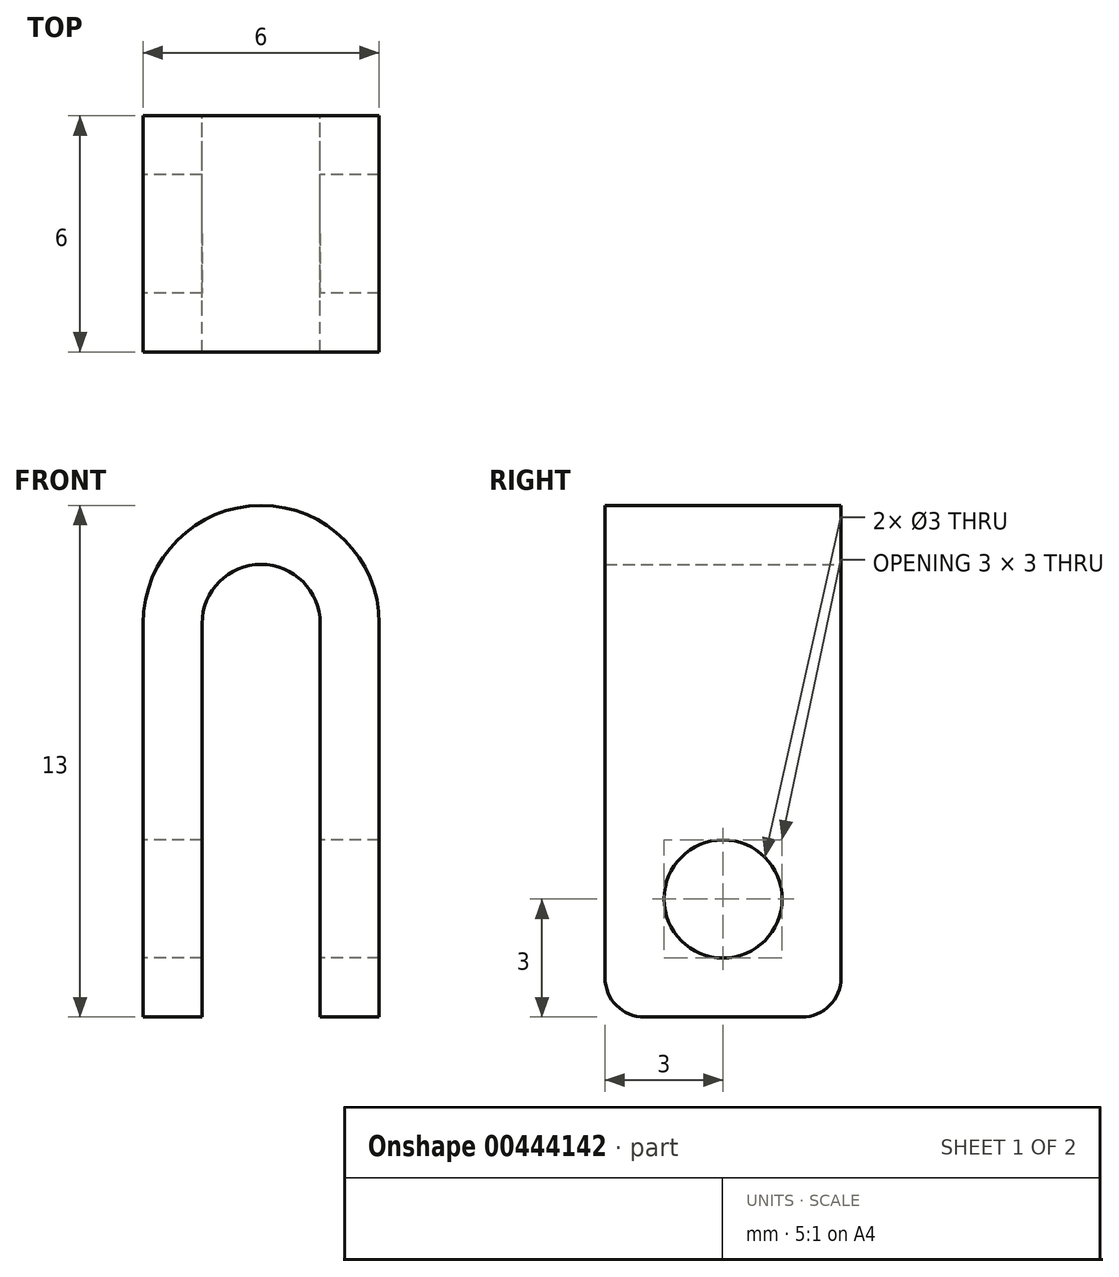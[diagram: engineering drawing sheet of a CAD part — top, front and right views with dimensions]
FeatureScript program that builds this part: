
annotation { "Feature Type Name" : "Feature", "Feature Type Description" : "" }
export const myFeature = defineFeature(function(context is Context, id is Id, definition is map)
    precondition{}
    {
        {
            var Q0;
            Q0=qCreatedBy(makeId("Front.planeOp"),FACE);
            var sketch = newSketch(context, id + "F0", { "sketchPlane" : qUnion([Q0])});
            skArc(sketch, "E0", {"start": v(-1.5, 0) * mm, "mid": v(0, 1.5) * mm, "end": v(1.5, 0) * mm});
            skArc(sketch, "E1", {"start": v(-3, 0) * mm, "mid": v(0, 3) * mm, "end": v(3, 0) * mm});
            skLineSegment(sketch, "E2", {"start": v(-1.5, 0) * mm, "end": v(-1.5, -10) * mm});
            skLineSegment(sketch, "E3", {"start": v(-3, -10) * mm, "end": v(-3, 0) * mm});
            skLineSegment(sketch, "E4", {"start": v(1.5, 0) * mm, "end": v(1.5, -10) * mm});
            skLineSegment(sketch, "E5", {"start": v(3, -10) * mm, "end": v(3, 0) * mm});
            skLineSegment(sketch, "E6", {"start": v(-3, -10) * mm, "end": v(-1.5, -10) * mm});
            skLineSegment(sketch, "E7", {"start": v(1.5, -10) * mm, "end": v(3, -10) * mm});
            skSolve(sketch);
        }
        {
            var Q0;
            Q0=makeQuery(id+"F0.imprint","IMPRINT",FACE,{"disambiguationData":[TD([[makeQuery(id+"F0.imprint","IMPRINT",EDGE,{"derivedFrom":sQuery(id+"F0.wireOp",EDGE,"E0")}),1.0]])]});
            var Q1;
            Q1=makeQuery(id+"F0.imprint","IMPRINT",FACE,{"disambiguationData":[TD([[makeQuery(id+"F0.imprint","IMPRINT",EDGE,{"derivedFrom":sQuery(id+"F0.wireOp",EDGE,"E0")}),-1.0]])]});
            var Q2;
            Q2=makeQuery(id+"F0.imprint","IMPRINT",FACE,{"disambiguationData":[TD([[makeQuery(id+"F0.imprint","IMPRINT",EDGE,{"derivedFrom":sQuery(id+"F0.wireOp",EDGE,"2HMxa7M1-go9X-fjSn-Mpx8-X3Mcg31AgzwF.bottom")}),-1.0]])]});
            var Q3;
            Q3=makeQuery(id+"F0.imprint","IMPRINT",FACE,{"disambiguationData":[TD([[makeQuery(id+"F0.imprint","IMPRINT",EDGE,{"derivedFrom":sQuery(id+"F0.wireOp",EDGE,"UYwaTrHf-vhDH-wfQa-s1mw-S1oxrttcXev8.bottom")}),1.0]])]});
            extrude(context, id + "F1", {"entities" : qUnion([Q0, Q1, Q2, Q3]), "depth" : 6 * mm});
        }
        {
            var Q0;
            Q0=makeQuery(id+"F1.opExtrude","SWEPT_FACE",FACE,{"disambiguationData":[OSD([sQuery(id+"F0.wireOp",EDGE,"E3")])]});
            var sketch = newSketch(context, id + "F2", { "sketchPlane" : qUnion([Q0])});
            skPoint(sketch, "E8", {"position": v(3, -7) * mm});
            skLineSegment(sketch, "E9.0.0", {"start": v(0, 0) * mm, "end": v(0, -10) * mm});
            skLineSegment(sketch, "E9.0.1", {"start": v(0, -10) * mm, "end": v(6, -10) * mm});
            skLineSegment(sketch, "E9.0.2", {"start": v(6, -10) * mm, "end": v(6, 0) * mm});
            skLineSegment(sketch, "E9.0.3", {"start": v(6, 0) * mm, "end": v(0, 0) * mm});
            skSolve(sketch);
        }
        {
            var Q0;
            Q0=sQuery(id+"F2.wireOp",VERTEX,"E8");
            var Q1;
            Q1=makeQuery(id+"F1.opExtrude","SWEPT_BODY",BODY,{"disambiguationData":[OSD([sQuery(id+"F0.wireOp",EDGE,"E1"),sQuery(id+"F0.wireOp",EDGE,"E2"),sQuery(id+"F0.wireOp",EDGE,"E3"),sQuery(id+"F0.wireOp",EDGE,"E4"),sQuery(id+"F0.wireOp",EDGE,"E5"),sQuery(id+"F0.wireOp",EDGE,"E6"),sQuery(id+"F0.wireOp",EDGE,"E7"),sQuery(id+"F0.wireOp",EDGE,"LvwC1Lki-g2hb-s0HK-j71i-HixQ3Io3APyM"),sQuery(id+"F0.wireOp",EDGE,"Cmuu76nB-nvyt-PSXK-WyLN-4q3TdGoNDzTt"),sQuery(id+"F0.wireOp",EDGE,"OvqNn00F-z49C-7cTw-GN2S-lB0Pj5r9IvEE")])]});
            hole(context, id + "F3", {"style" : HoleStyle.SIMPLE, "endStyle" : HoleEndStyle.THROUGH, "holeDiameter" : 3 * mm, "isTappedThrough" : true, "tappedDepth" : 12 * mm, "tapClearance" : 3, "locations" : qUnion([Q0]), "scope" : qUnion([Q1])});
        }
        {
            var Q0;
            Q0=makeQuery(id+"F1.opExtrude","CAP_EDGE",EDGE,{"disambiguationData":[OSD([sQuery(id+"F0.wireOp",EDGE,"E6")])],"isStart":false});
            var Q1;
            Q1=makeQuery(id+"F1.opExtrude","CAP_EDGE",EDGE,{"disambiguationData":[OSD([sQuery(id+"F0.wireOp",EDGE,"E7")])],"isStart":false});
            var Q2;
            Q2=makeQuery(id+"F1.opExtrude","CAP_EDGE",EDGE,{"disambiguationData":[OSD([sQuery(id+"F0.wireOp",EDGE,"E7")])],"isStart":true});
            var Q3;
            Q3=makeQuery(id+"F1.opExtrude","CAP_EDGE",EDGE,{"disambiguationData":[OSD([sQuery(id+"F0.wireOp",EDGE,"E6")])],"isStart":true});
            fillet(context, id + "F4", {"entities" : qUnion([Q0, Q1, Q2, Q3]), "radius" : 1 * mm, "tangentPropagation" : true, "allowEdgeOverflow" : false});
        }
    });
